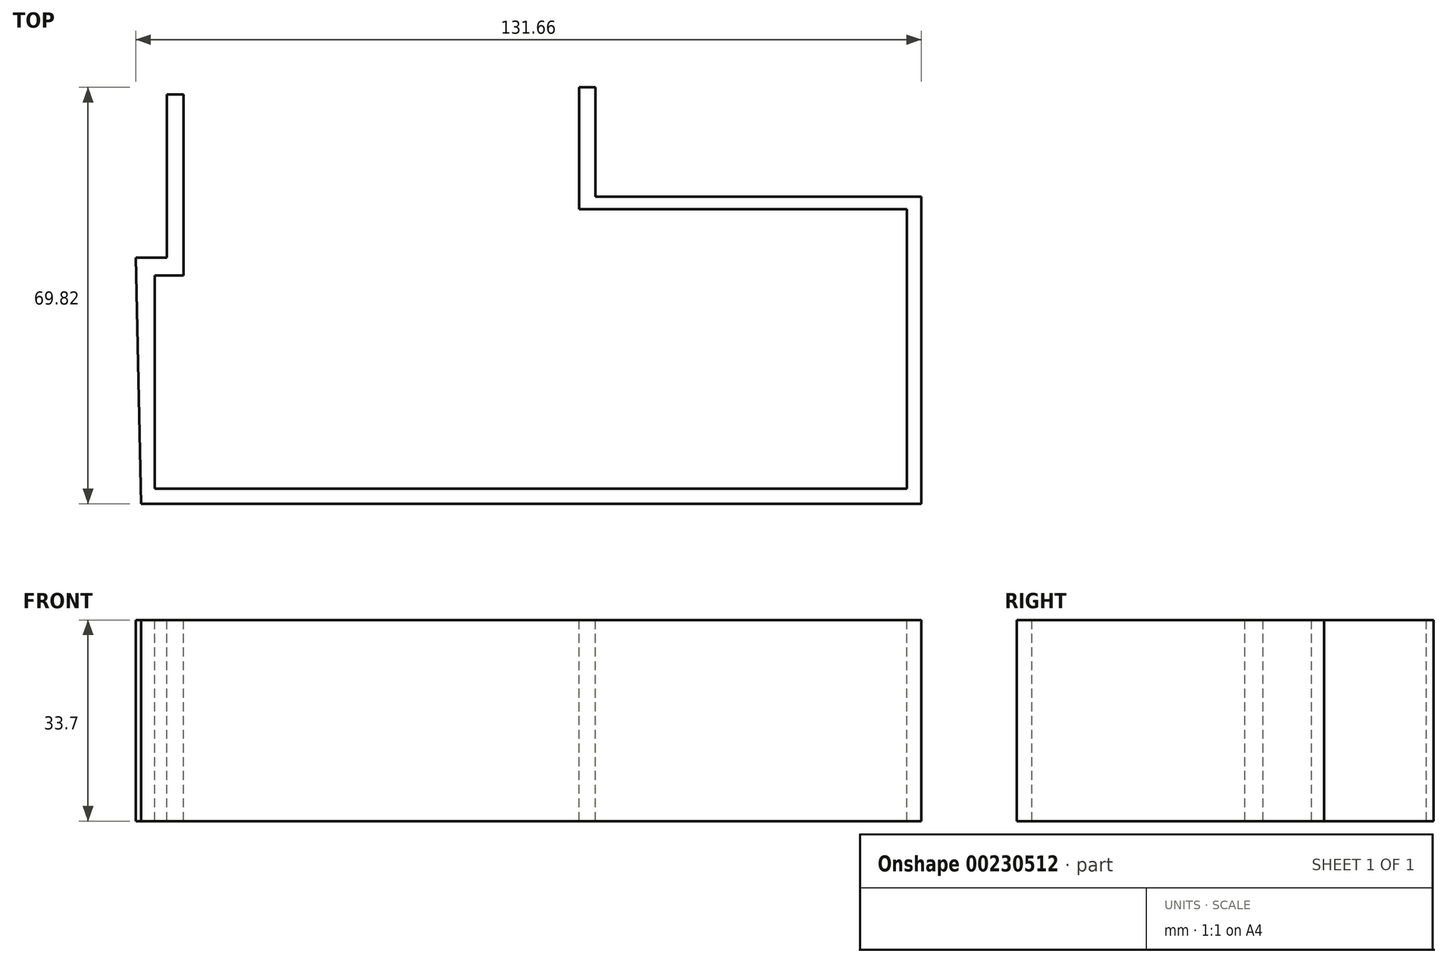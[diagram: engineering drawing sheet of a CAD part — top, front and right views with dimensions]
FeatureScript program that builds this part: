
annotation { "Feature Type Name" : "Feature", "Feature Type Description" : "" }
export const myFeature = defineFeature(function(context is Context, id is Id, definition is map)
    precondition{}
    {
        {
            var Q0;
            Q0=qCreatedBy(makeId("Top.planeOp"),FACE);
            var sketch = newSketch(context, id + "F0", { "sketchPlane" : qUnion([Q0])});
            skLineSegment(sketch, "E0", {"start": v(-58.73, -45.41) * mm, "end": v(67.3, -45.41) * mm});
            skLineSegment(sketch, "E1", {"start": v(67.3, -45.41) * mm, "end": v(67.3, 1.48) * mm});
            skLineSegment(sketch, "E2", {"start": v(67.3, 1.48) * mm, "end": v(12.37, 1.48) * mm});
            skLineSegment(sketch, "E3", {"start": v(12.37, 1.48) * mm, "end": v(12.37, 21.89) * mm});
            skLineSegment(sketch, "E4", {"start": v(-58.73, -45.41) * mm, "end": v(-58.73, -9.68) * mm});
            skLineSegment(sketch, "E5", {"start": v(-58.73, -9.68) * mm, "end": v(-53.92, -9.68) * mm});
            skLineSegment(sketch, "E6", {"start": v(-53.92, -9.68) * mm, "end": v(-53.92, 20.7) * mm});
            skLineSegment(sketch, "E7", {"start": v(-61, -47.93) * mm, "end": v(69.74, -47.93) * mm});
            skLineSegment(sketch, "E8", {"start": v(69.74, -47.93) * mm, "end": v(69.74, 3.55) * mm});
            skLineSegment(sketch, "E9", {"start": v(69.74, 3.55) * mm, "end": v(15.12, 3.55) * mm});
            skLineSegment(sketch, "E10", {"start": v(15.12, 3.55) * mm, "end": v(15.12, 21.89) * mm});
            skLineSegment(sketch, "E11", {"start": v(15.12, 21.89) * mm, "end": v(12.37, 21.89) * mm});
            skLineSegment(sketch, "E12", {"start": v(-53.92, 20.7) * mm, "end": v(-56.67, 20.7) * mm});
            skLineSegment(sketch, "E13", {"start": v(-56.67, 20.7) * mm, "end": v(-56.67, -6.68) * mm});
            skLineSegment(sketch, "E14", {"start": v(-56.67, -6.68) * mm, "end": v(-61.92, -6.68) * mm});
            skLineSegment(sketch, "E15", {"start": v(-61.92, -6.68) * mm, "end": v(-61, -47.93) * mm});
            skSolve(sketch);
        }
        {
            var Q0;
            Q0 = qSketchRegion(id + "F0", true);
            extrude(context, id + "F1", {"entities" : qUnion([Q0]), "oppositeDirection" : true, "depth" : 33.7 * mm});
        }
    });
